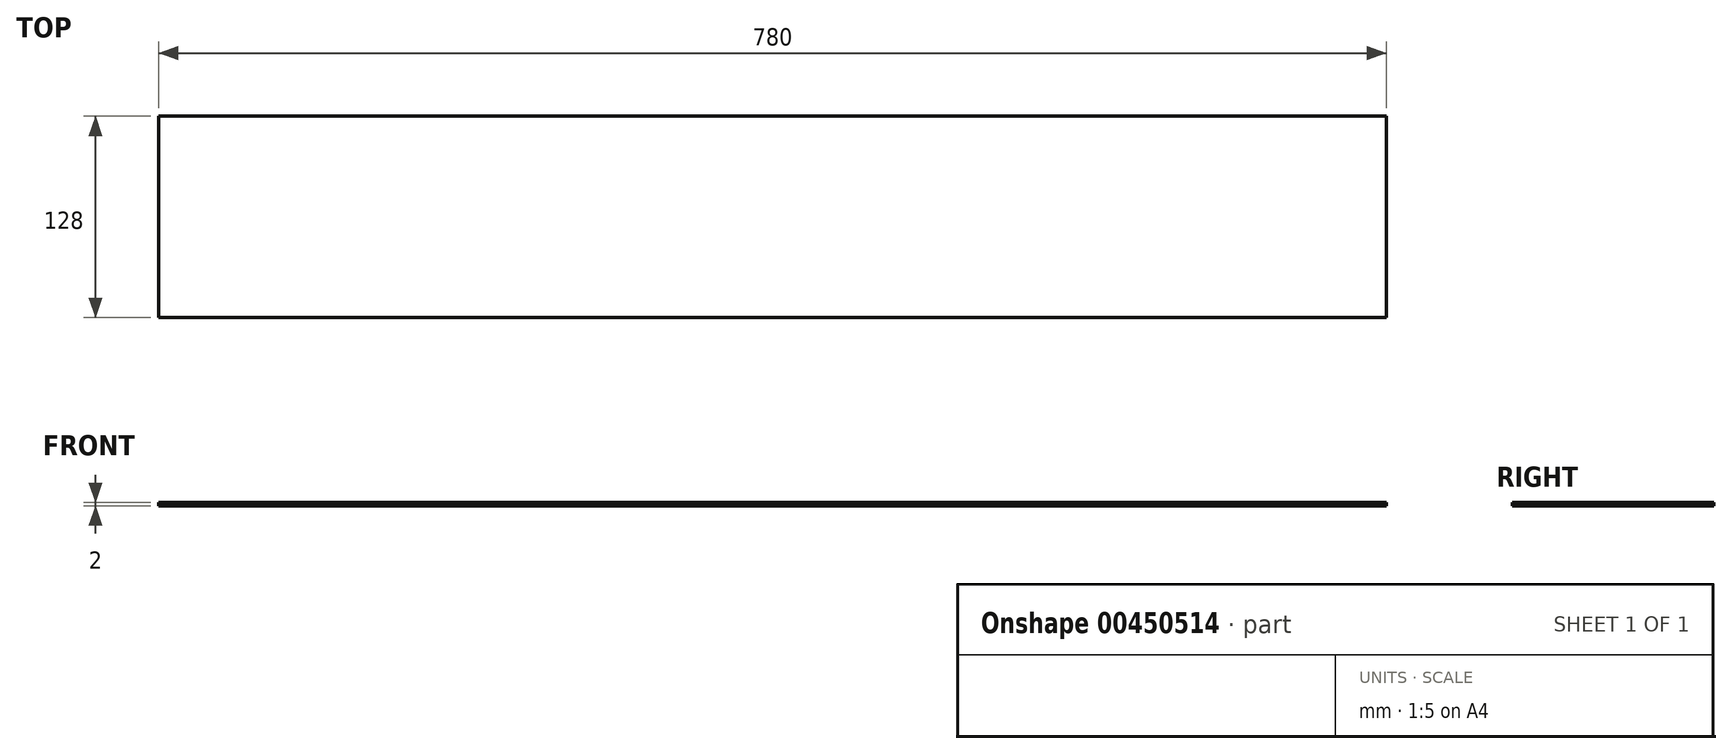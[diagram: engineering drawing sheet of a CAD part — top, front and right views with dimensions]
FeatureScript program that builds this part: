
annotation { "Feature Type Name" : "Feature", "Feature Type Description" : "" }
export const myFeature = defineFeature(function(context is Context, id is Id, definition is map)
    precondition{}
    {
        {
            var Q0;
            Q0=qCreatedBy(makeId("Top.planeOp"),FACE);
            var sketch = newSketch(context, id + "F0", { "sketchPlane" : qUnion([Q0])});
            skLineSegment(sketch, "E0.bottom", {"start": v(-390, 64) * mm, "end": v(390, 64) * mm});
            skLineSegment(sketch, "E0.top", {"start": v(-390, -64) * mm, "end": v(390, -64) * mm});
            skLineSegment(sketch, "E0.left", {"start": v(-390, 64) * mm, "end": v(-390, -64) * mm});
            skLineSegment(sketch, "E0.right", {"start": v(390, 64) * mm, "end": v(390, -64) * mm});
            skPoint(sketch, "E0.middle", {"position": v(0, 0) * mm});
            skSolve(sketch);
        }
        {
            var Q0;
            Q0=makeQuery(id+"F0.imprint","IMPRINT",FACE,{"disambiguationData":[TD([[makeQuery(id+"F0.imprint","IMPRINT",EDGE,{"derivedFrom":sQuery(id+"F0.wireOp",EDGE,"E0.bottom")}),-1.0]])]});
            extrude(context, id + "F1", {"entities" : qUnion([Q0]), "endBound" : BoundingType.SYMMETRIC, "depth" : 2 * mm});
        }
    });
